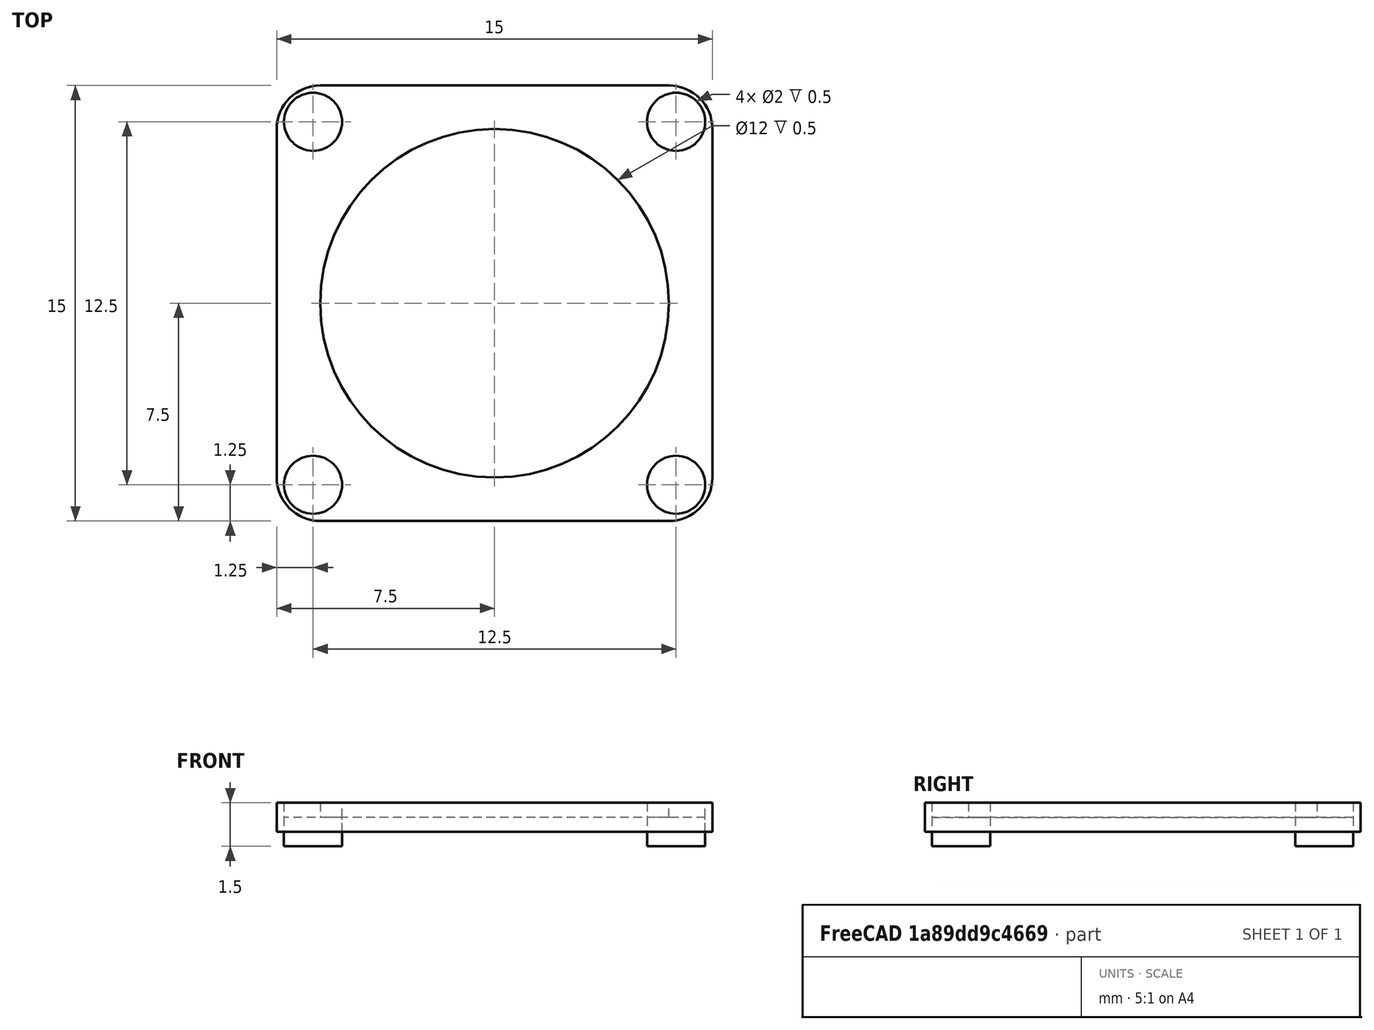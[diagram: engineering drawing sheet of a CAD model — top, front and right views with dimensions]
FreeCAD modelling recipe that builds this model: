
FCSTD DOCUMENT  (FreeCAD 1.0RUnknown)
Label: coasters
License: All rights reserved
LicenseURL: https://en.wikipedia.org/wiki/All_rights_reserved
objects: Part::Cylinder×9, Part::Cut×5, Part::Box×1, Part::Fillet×1, App::DocumentObjectGroup×1
note: 16 computed .brp shape members not serialized (recipe doc carries the construction recipe); baked Part::Feature solids carry a one-line shape summary decoded from their .brp

FEATURE [Part::Box] Box  label="Platform"
  AttacherType = Attacher::AttachEngine3D
  Height = 1
  Length = 15
  Width = 15
FEATURE [Part::Cylinder] Cylinder
  Angle = 360
  AttacherType = Attacher::AttachEngine3D
  FirstAngle = 0
  Height = 1
  Placement = pos=(1.25,1.25,0.5) rot=(0,0,1;0rad)
  Radius = 1
  SecondAngle = 0
FEATURE [Part::Cylinder] Cylinder002  label="Cylinder2"
  Angle = 360
  AttacherType = Attacher::AttachEngine3D
  FirstAngle = 0
  Height = 1
  Placement = pos=(13.75,1.25,0.5) rot=(0,0,1;0rad)
  Radius = 1
  SecondAngle = 0
FEATURE [Part::Cylinder] Cylinder003  label="Cylinder3"
  Angle = 360
  AttacherType = Attacher::AttachEngine3D
  FirstAngle = 0
  Height = 1
  Placement = pos=(13.75,13.75,0.5) rot=(0,0,1;0rad)
  Radius = 1
  SecondAngle = 0
FEATURE [Part::Cylinder] Cylinder007  label="Cylinder4"
  Angle = 360
  AttacherType = Attacher::AttachEngine3D
  FirstAngle = 0
  Height = 1
  Placement = pos=(1.25,13.75,0.5) rot=(0,0,1;0rad)
  Radius = 1
  SecondAngle = 0
FEATURE [Part::Cylinder] Cylinder008  label="Foot 4"
  Angle = 360
  AttacherType = Attacher::AttachEngine3D
  FirstAngle = 0
  Height = 1
  Placement = pos=(1.25,1.25,-0.5) rot=(0,0,1;0rad)
  Radius = 1
  SecondAngle = 0
FEATURE [Part::Cylinder] Cylinder009  label="Foot 3"
  Angle = 360
  AttacherType = Attacher::AttachEngine3D
  FirstAngle = 0
  Height = 1
  Placement = pos=(13.75,1.25,-0.5) rot=(0,0,1;0rad)
  Radius = 1
  SecondAngle = 0
FEATURE [Part::Cylinder] Cylinder010  label="Foot 1"
  Angle = 360
  AttacherType = Attacher::AttachEngine3D
  FirstAngle = 0
  Height = 1
  Placement = pos=(13.75,13.75,-0.5) rot=(0,0,1;0rad)
  Radius = 1
  SecondAngle = 0
FEATURE [Part::Cylinder] Cylinder011  label="Foot 2"
  Angle = 360
  AttacherType = Attacher::AttachEngine3D
  FirstAngle = 0
  Height = 1
  Placement = pos=(1.25,13.75,-0.5) rot=(0,0,1;0rad)
  Radius = 1
  SecondAngle = 0
FEATURE [Part::Cut] Cut
  Base = -> Box
  Tool = -> Cylinder
FEATURE [Part::Cut] Cut001
  Base = -> Cut
  Tool = -> Cylinder002
FEATURE [Part::Cut] Cut002
  Base = -> Cut001
  Tool = -> Cylinder003
FEATURE [Part::Cut] Cut003
  Base = -> Cut002
  Tool = -> Cylinder007
FEATURE [Part::Cylinder] Cylinder012
  Angle = 360
  AttacherType = Attacher::AttachEngine3D
  FirstAngle = 0
  Height = 1
  Placement = pos=(7.5,7.5,0.5) rot=(0,0,1;0rad)
  Radius = 6
  SecondAngle = 0
FEATURE [Part::Cut] Cut004
  Base = -> Cut003
  Tool = -> Cylinder012
FEATURE [Part::Fillet] Fillet  label="Body"
  Base = -> Cut004
  EdgeLinks = -> Cut004 [Edge1,Edge3,Edge6,Edge16]
  Edges = 4 edges r=1.5: [Edge1,Edge3,Edge6,Edge16]
FEATURE [App::DocumentObjectGroup] Group  label="Feet"
  Group = -> [Cylinder010,Cylinder011,Cylinder009,Cylinder008]
